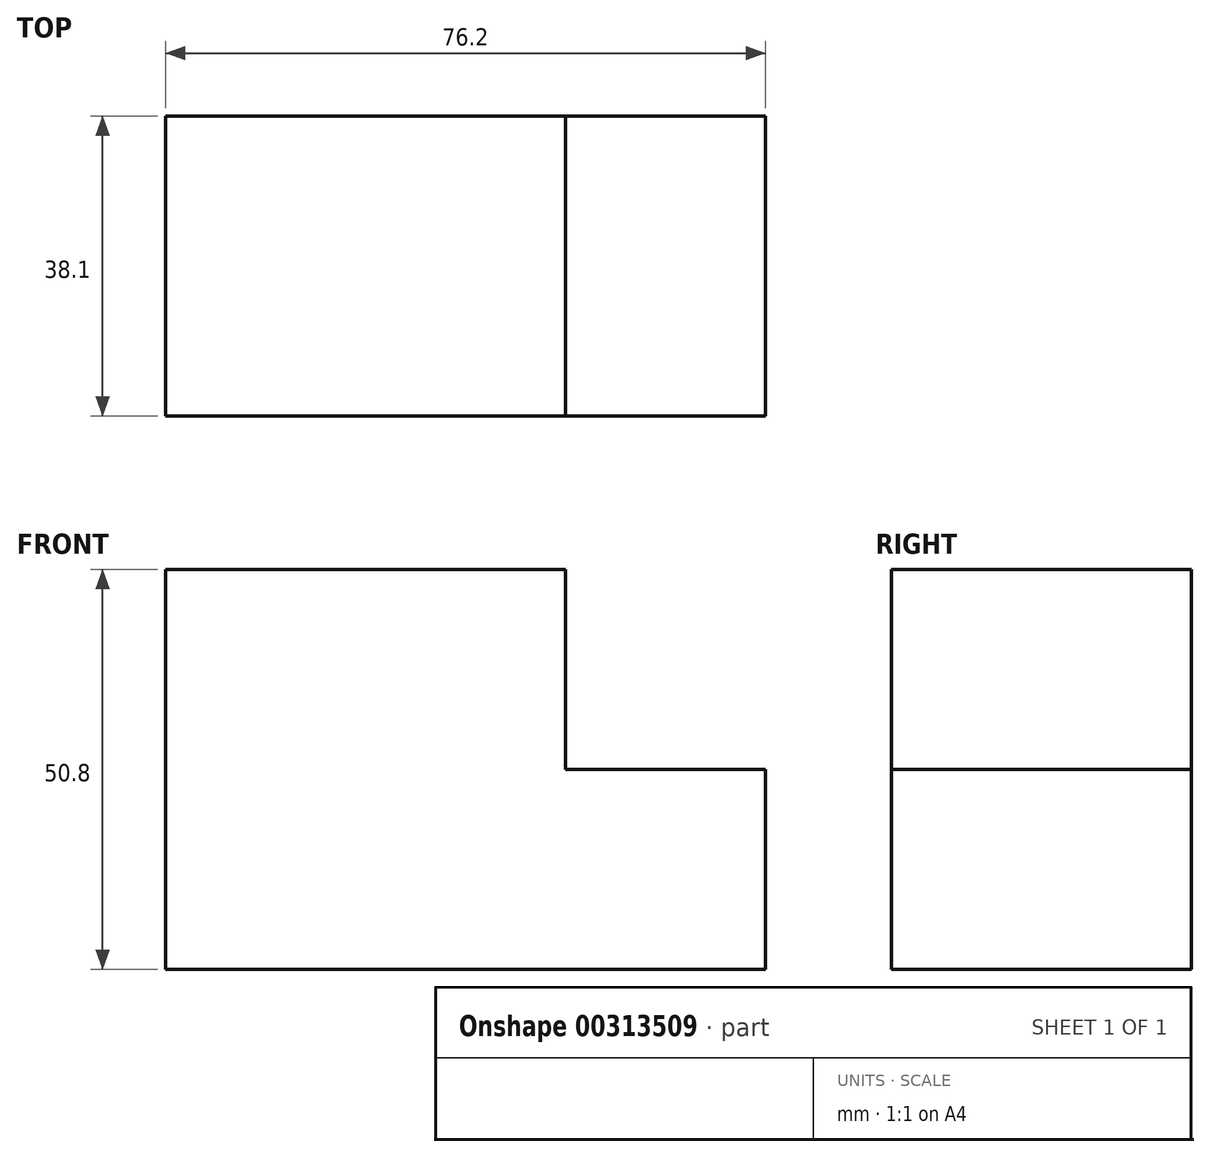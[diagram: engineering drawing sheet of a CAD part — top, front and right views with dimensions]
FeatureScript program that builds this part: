
annotation { "Feature Type Name" : "Feature", "Feature Type Description" : "" }
export const myFeature = defineFeature(function(context is Context, id is Id, definition is map)
    precondition{}
    {
        {
            var Q0;
            Q0=qCreatedBy(makeId("Front.planeOp"),FACE);
            var sketch = newSketch(context, id + "F0", { "sketchPlane" : qUnion([Q0])});
            skLineSegment(sketch, "E0", {"start": v(-39.02, -43.89) * mm, "end": v(37.18, -43.89) * mm});
            skLineSegment(sketch, "E1", {"start": v(37.18, -43.89) * mm, "end": v(37.18, -18.49) * mm});
            skLineSegment(sketch, "E2", {"start": v(37.18, -18.49) * mm, "end": v(11.78, -18.49) * mm});
            skLineSegment(sketch, "E3", {"start": v(11.78, -18.49) * mm, "end": v(11.78, 6.91) * mm});
            skLineSegment(sketch, "E4", {"start": v(11.78, 6.91) * mm, "end": v(-39.02, 6.91) * mm});
            skLineSegment(sketch, "E5", {"start": v(-39.02, 6.91) * mm, "end": v(-39.02, -43.89) * mm});
            skSolve(sketch);
        }
        {
            var Q0;
            Q0=makeQuery(id+"F0.imprint","IMPRINT",FACE,{"disambiguationData":[TD([[makeQuery(id+"F0.imprint","IMPRINT",EDGE,{"derivedFrom":sQuery(id+"F0.wireOp",EDGE,"E0")}),1.0]])]});
            extrude(context, id + "F1", {"entities" : qUnion([Q0]), "depth" : 38.1 * mm});
        }
    });
